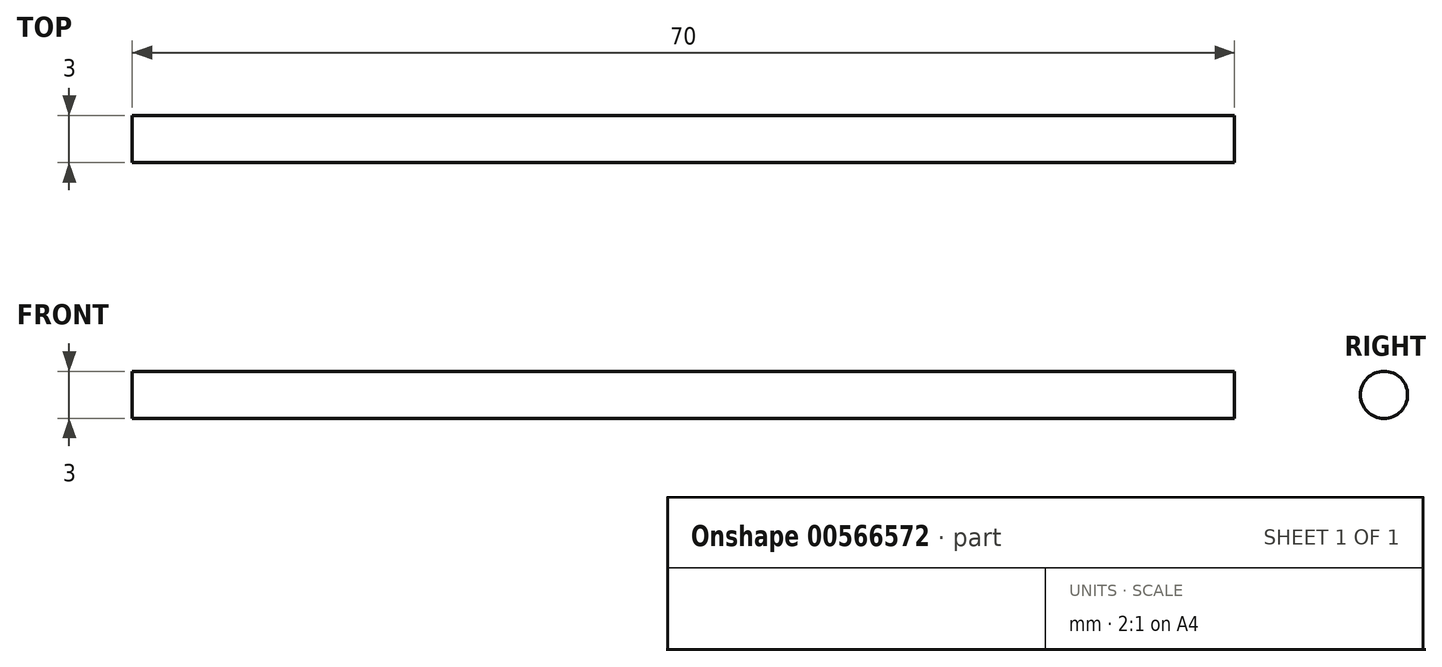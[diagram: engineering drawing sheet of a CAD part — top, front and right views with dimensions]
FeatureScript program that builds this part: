
annotation { "Feature Type Name" : "Feature", "Feature Type Description" : "" }
export const myFeature = defineFeature(function(context is Context, id is Id, definition is map)
    precondition{}
    {
        {
            var Q0;
            Q0=qCreatedBy(makeId("Right.planeOp"),FACE);
            var sketch = newSketch(context, id + "F0", { "sketchPlane" : qUnion([Q0])});
            skCircle(sketch, "E0", {"center": v(0, 0) * mm, "radius": 1.5 * mm});
            skSolve(sketch);
        }
        {
            var Q0;
            Q0 = qSketchRegion(id + "F0", true);
            extrude(context, id + "F1", {"entities" : qUnion([Q0]), "depth" : 70 * mm, "offsetDistance" : 25 * mm});
        }
    });
